# Revit family: Hager-Gamma-IP30-syst-NoHosted-CH-en
name_source: partatom
category: Electrical Equipment
units: mm (PartAtom-declared; Revit-internal decimal feet)

## family parameters
Always vertical = Yes
Cut with Voids When Loaded = No
Panel Configuration = Two Columns, Circuits Across
Part Type = Panelboard
Room Calculation Point = No
Round Connector Dimension = Use Diameter
Shared = No
Work Plane-Based = Yes

## types (4) — shared parameters
Default Elevation = 1219 mm
EF000003 - Mounting method = EV000384 - Surface mounted (plaster)
EF000007 - Colour = EV000202 - White
EF000008 - Width = 250 mm  [stored 0.82021 ft]
EF000049 - Depth = 103 mm  [stored 0.337927 ft]
EF000116 - RAL-number = 9010
EF000118 - With mounting plate = No
EF000339 - Type of cover = EV001012 - Cover
EF001062 - EMC-version = No
EF001088 - Extension possible = Yes
EF001134 - DIN-rail = Yes
EF001596 - Material housing = EV000139 - Plastic
EF002950 - Width in number of modular spacings = 13
EF004462 - Type of closure = EV000154 - Other
EF005474 - Degree of protection (IP) = EV006410 - IP30
EF006244 - Transparent cover/door = No
EF006306 - With lock = No
EF009212 - Cover model = EV009916 - With notch
HG000001 - Number of columns = 1
HG000002 - With door or cover = No
HG000003 - Range = Gamma
HG000005 - Thickness = 3 mm  [stored 0.00984252 ft]
HG000006 - Flush mounted = No
HG000009 - Double swing door = No
HG000010 - Asymmetric doors = No
HG000011 - Empty rows from bottom = No
HG000017 - Distance between poles = 18 mm  [stored 0.0590551 ft]
Manufacturer = Hager
Type Comments = Gamma
zero-valued in all types: EF000218 - Built-in depth, EF000332 - Built-in height, EF000846 - Built-in width, EF001131 - Internal depth, HG000007 - Number of empty columns, HG000008 - Number of empty rows

## per-type parameters (varying)
| type | EF000040 - Height | EF000266 - Number of rows | EF015776 - Earthing terminal block | EF015777 - Neutral terminal block | EF015941 - Signal passing door | HG000004 - Manufacturer reference | Model |
| Surface mounted IP30 W250 H250 D103 13 Modular spacings - GD113G | 250 mm  [stored 0.82021 ft] | 1 | Yes | Yes | Yes | GD113G | GD113G |
| Surface mounted IP30 W250 H375 D103 13 Modular spacings - GD213G | 375 mm | 2 | No | No | No | GD213G | GD213G |
| Surface mounted IP30 W250 H500 D103 13 Modular spacings - GD313G | 500 mm  [stored 1.64042 ft] | 3 | No | No | No | GD313G | GD313G |
| Surface mounted IP30 W250 H625 D103 13 Modular spacings - GD413G | 625 mm  [stored 2.05052 ft] | 4 | No | No | No | GD413G | GD413G |

note: [stored X ft] marks values corroborated as IEEE doubles in the binary element streams (Revit-internal decimal feet)

## geometry (parser evidence)
native form markers: Sweep x14
no freeform markers — native parametric forms only
